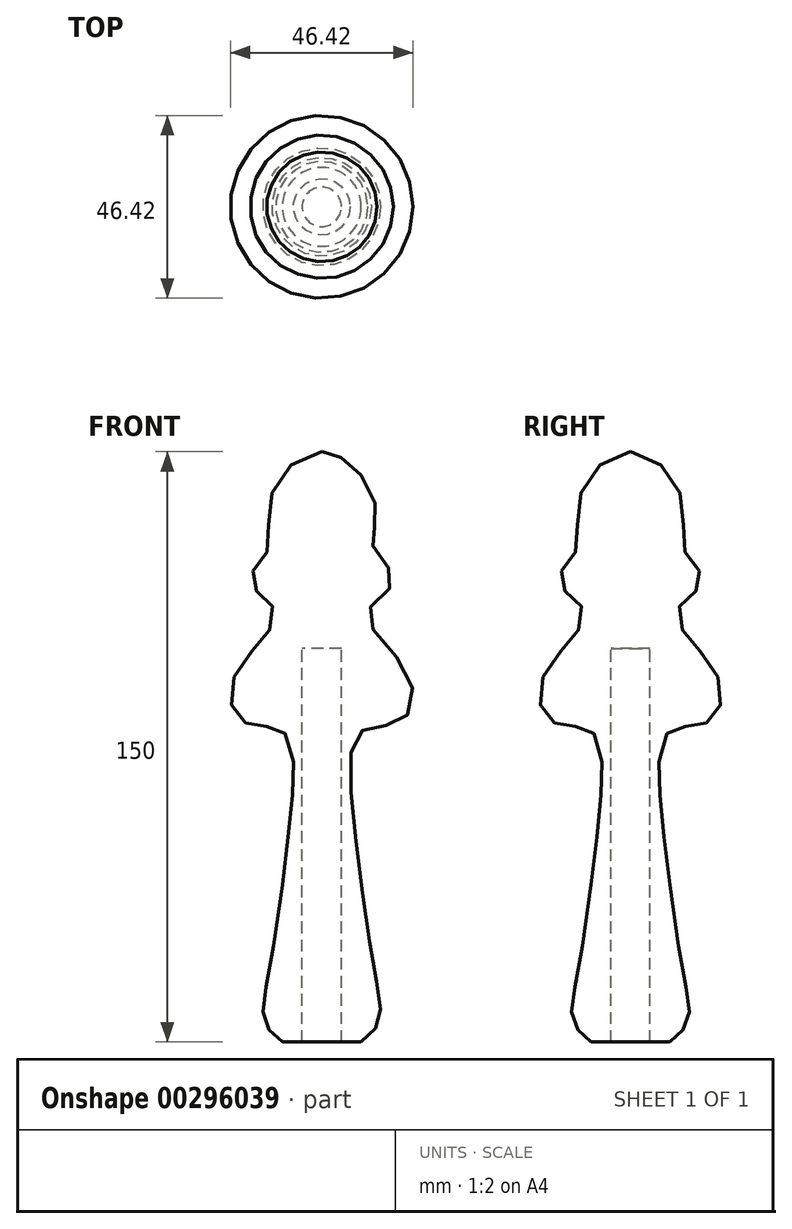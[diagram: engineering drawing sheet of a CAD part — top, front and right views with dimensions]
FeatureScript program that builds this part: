
annotation { "Feature Type Name" : "Feature", "Feature Type Description" : "" }
export const myFeature = defineFeature(function(context is Context, id is Id, definition is map)
    precondition{}
    {
        {
            var Q0;
            Q0=qCreatedBy(makeId("Front.planeOp"),FACE);
            var sketch = newSketch(context, id + "F0", { "sketchPlane" : qUnion([Q0])});
            skFitSpline(sketch, "E0", {"points": [v(10, 0) * mm, v(14.5, 4.95) * mm, v(13.6, 16.66) * mm, v(8, 57.38) * mm, v(10, 79) * mm, v(20, 81.44) * mm, v(22, 93.4) * mm, v(11.64, 108.96) * mm, v(18.17, 117.1) * mm, v(12.76, 126.55) * mm, v(13.98, 133.8) * mm, v(7.3, 146.95) * mm, v(0, 150) * mm], "startDerivative": vector(87.17, 68.86) * mm, "endDerivative": vector(-107.03, 18.27) * mm});
            skLineSegment(sketch, "E1", {"start": v(0, 0) * mm, "end": v(0, 150) * mm, "construction": true});
            skLineSegment(sketch, "E2", {"start": v(5, 0) * mm, "end": v(5, 100) * mm});
            skPoint(sketch, "E2.endSnap0", {"position": v(5, 0) * mm});
            skLineSegment(sketch, "E3", {"start": v(5, 100) * mm, "end": v(0, 100) * mm});
            skLineSegment(sketch, "E4", {"start": v(10, 0) * mm, "end": v(5, 0) * mm});
            skSolve(sketch);
        }
        {
            var Q0;
            Q0=sQuery(id+"F0.wireOp",EDGE,"E0");
            var Q1;
            Q1=sQuery(id+"F0.wireOp",EDGE,"E4");
            var Q2;
            Q2=sQuery(id+"F0.wireOp",EDGE,"E2");
            var Q3;
            Q3=sQuery(id+"F0.wireOp",EDGE,"E3");
            var Q4;
            Q4=sQuery(id+"F0.wireOp",EDGE,"E1");
            revolve(context, id + "F1", {"bodyType" : ToolBodyType.SURFACE, "surfaceEntities" : qUnion([Q0, Q1, Q2, Q3]), "axis" : qUnion([Q4]), "revolveType" : RevolveType.FULL});
        }
    });
